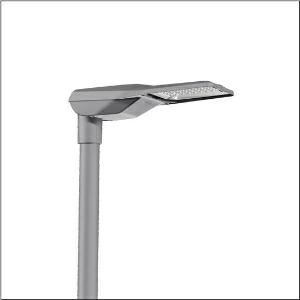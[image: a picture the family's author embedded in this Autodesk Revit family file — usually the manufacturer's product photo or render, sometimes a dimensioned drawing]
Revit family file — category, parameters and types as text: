
# Revit family: streetlight_sl_21_iq_mini___stw1_0a_5xe2e41g08gb_cbe1
name_source: partatom
category: Lighting Fixtures
units: mm (PartAtom-declared; Revit-internal decimal feet)

## family parameters
Cut with Voids When Loaded = No
Host = Face
Light Source = No
Part Type = Normal
Room Calculation Point = No
Round Connector Dimension = Use Diameter
Shared = No

## types (1)
- --- (1 x LED, 5920 lm, 37.1 W, 4000K)
    Apparent Load = 37 VA
    CIE Flux Codes = 38 75 98 100 100
    Color Rendering = 70
    Color Temperature = 4000K
    Default Elevation = 1800 mm
    Description = Streetlight SL 21 iQ mini, mast luminaire, primary light control with lens, of PMMA, primary optical cover: cover, of toughened safety glass, transparent, light distribution: STW1.0a, light emission: direct distribution, primary light characteristic: asymmetric, installation type: post-top, side-entry, LED, High Power LED, rated luminous flux: 5.920lm, luminous efficacy: 160lm/W, light colour: 740, colour temperature: 4000K, control: Street-Remote, Auto-Match, Temp-Guard, Lumen-Switch, Night-Set, Smart-Wire, Light-Fading, Desk-Remote (wireless, voltage-free reading and setting of iQ features in the workshop via application-optimized NFC function/RFID function), optimised constant luminous flux control (CLO 2.0), presetting dimming linear, mains connection: 220..240V, AC, 50/60Hz, start of lifetime: 37W, end of service life: 39W, reduction: 18W, luminaire housing, of diecast aluminium, powder-coated, Siteco® metallic grey (DB 702S), corrosivity category C5 mid according to DIN EN ISO 12944, please order mast flange separately, inclination adjustable: 0°, 5°, 10°, 15°, sealing non-destructively replaceable, multi-level sealing system, length: 628mm, width: 235mm, height: 110mm, mast flange for spigot size: 42mm (side-entry): 5XC10008XM4, 60/48mm (side-entry/post-top): 5XC10108XM2, 76/60mm (side-entry/post-top): 5XC10108XM1, protection rating (complete): IP66, insulation class (complete): insulation class II (safety insulation), certification: CE, ENEC, ENEC+, VDE, impact resistance: IK09, permissible operating ambient temperature for outdoor applications: -40..+50°C, standard-compliant lighting for roads and squares, packaging unit: 1 piece

Light Distribution: STW1.0a
    Height = 110 mm
    Lamp = 1 x LED
    Lamp Light Flux = 5920 lm
    Lamp Power = 37.1 W
    Lamp count = 1
    Length = 625 mm
    Luminous efficacy = 160 lm/W
    Manufacturer = Siteco
    ModVariant = No
    Model = 5XE2E41G08GB
    Number of Poles = 1
    OnlyDefault = Yes
    Power Factor = 1
    Product Name = Streetlight SL 21 iQ mini | STW1.0a
    Product group = mast luminaire | pylon top
    ProductGroupID = 6100
    Protection Class = Protection class II
    Protection Degree = IP 66
    RLX_Detail_Level = 1
    RLX_Emergency_Light_Flux = 0 lm
    RLX_Emergency_Type = 0
    RLX_Emergency_Type_DB = No
    RlxData = <blob elided: 92017 chars, md5=edb69124>
    Socket = socket
    Standby Power = 0 W
    System Light Flux = 5920 lm
    System Power = 37 W
    Type Comments = factory setting: luminous flux: 100 % | dim-lin: 254 | 385 mA
    Type Image = l_1003519.jpg
    URL = http://relux.com
    VarID = @adj_120981
    Voltage = 0 V
    Weight = 0.00 kg
    Width = 234 mm

## geometry (parser evidence)
native form markers: Blend x4, Sweep x12
no freeform markers — native parametric forms only
